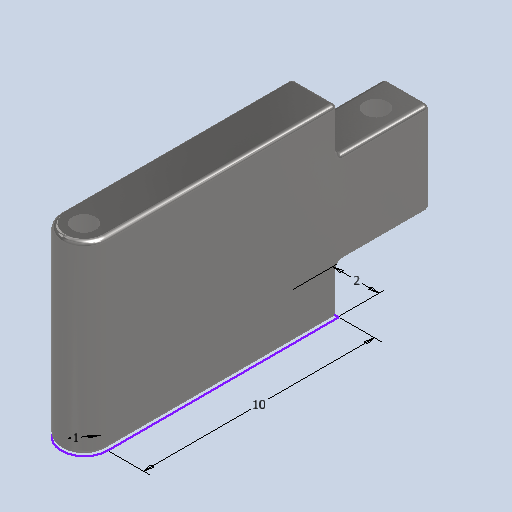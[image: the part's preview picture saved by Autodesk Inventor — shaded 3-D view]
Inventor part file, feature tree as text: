
AUTODESK INVENTOR PART (.ipt)
format: ipt  version: 2022 (Build 260153000, 153)  size: 153,088 bytes
history: native  units: mm (DEFAULTED — no unit token found)
features: extrude x3, sketch x3, fillet x1
ambient origin geometry x8: Origin, YZ Plane, XZ Plane, XY Plane, X Axis, Y Axis, Z Axis, Center Point
bodies: Solid1 (feature_tree)
feature tree (7):
  extrude  "Extrusion1"  Depth=10.0mm
  extrude  "Extrusion2"  Depth=40.0mm
  extrude  "Extrusion3"  Depth=10.0mm
  fillet  "Fillet1"  Radius=40.0mm
  sketch  "Sketch1"  dims[d1=10.0mm d2=100.0mm]
  sketch  "Sketch2"  dims[d3=80.0mm d4=0.0mm d5=40.0mm]
  sketch  "Sketch3"  dims[d6=40.0mm d7=0.0mm d8=10.0mm d9=40.0mm d10=0.0mm d11=2.0mm d12=20.0mm]
